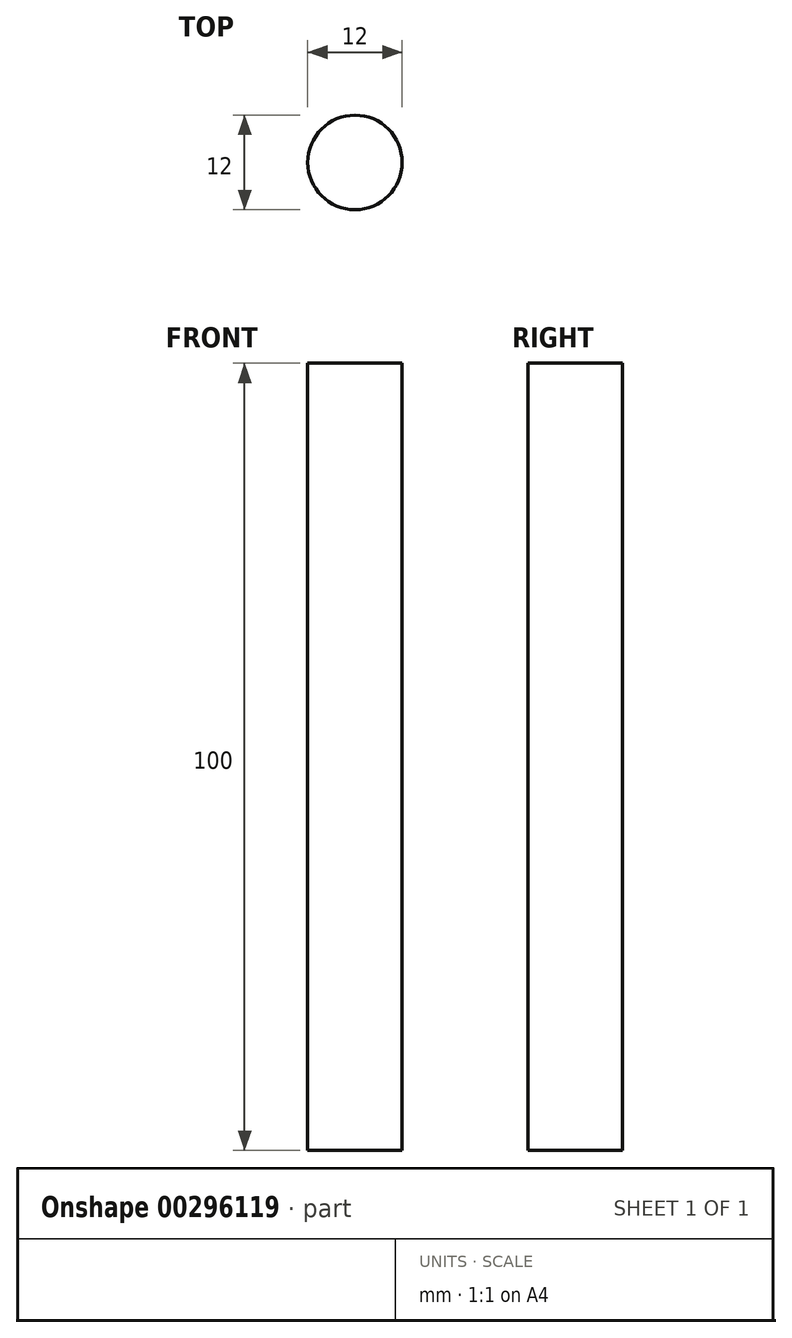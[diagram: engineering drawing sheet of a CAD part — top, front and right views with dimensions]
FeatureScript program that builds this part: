
annotation { "Feature Type Name" : "Feature", "Feature Type Description" : "" }
export const myFeature = defineFeature(function(context is Context, id is Id, definition is map)
    precondition{}
    {
        {
            var Q0;
            Q0=qCreatedBy(makeId("Top.planeOp"),FACE);
            var sketch = newSketch(context, id + "F0", { "sketchPlane" : qUnion([Q0])});
            skCircle(sketch, "E0", {"center": v(0, 0) * mm, "radius": 6 * mm});
            skSolve(sketch);
        }
        {
            var Q0;
            Q0=makeQuery(id+"F0.imprint","IMPRINT",FACE,{"disambiguationData":[TD([[makeQuery(id+"F0.imprint","IMPRINT",EDGE,{"derivedFrom":sQuery(id+"F0.wireOp",EDGE,"E0")}),1.0]])]});
            extrude(context, id + "F1", {"entities" : qUnion([Q0]), "depth" : 100 * mm, "offsetDistance" : 25 * mm});
        }
    });
